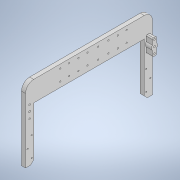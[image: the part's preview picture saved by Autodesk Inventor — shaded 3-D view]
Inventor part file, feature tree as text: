
AUTODESK INVENTOR PART (.ipt)
format: ipt  version: 2020.1 (Build 241239000, 239)  size: 278,528 bytes
history: native  units: in
note: dims shown in document units (in); Inventor stores cm internally (conversion verified against a paired STEP export)
features: sketch x11, extrude x8, mirror x2, chamfer x1, fillet x1, hole x1, projected_geometry x1
ambient origin geometry x8: Origin, YZ Plane, XZ Plane, XY Plane, X Axis, Y Axis, Z Axis, Center Point
bodies: Solid1 (feature_tree)
feature tree (25):
  extrude  "Extrusion1"  Depth=6.44in
  extrude  "Extrusion3"  Depth=0.5in TaperAngle=0.0deg
  chamfer  "Chamfer1"  Distance=1.0in
  extrude  "Extrusion4"  Depth=0.75in
  mirror  "Mirror2"
  extrude  "Extrusion5"  Depth=2.5in
  fillet  "Fillet2"  Radius=1.0in
  extrude  "Extrusion6"  Depth=0.5in
  sketch  "Sketch9"  dims[d19=0.75in d20=0.0in d21=2.5in d22=1.0in d23=0.0in]
  extrude  "Extrusion8"  Depth=0.125in
  mirror  "Mirror3"
  extrude  "Extrusion9"  Depth=0.25in
  extrude  "Extrusion10"  Depth=0.25in
  hole  "Hole1"  [1 undecoded]
  sketch  "Sketch14"  dims[d32=0.75in d33=0.0in d47=0.25in d48=10.0in d49=0.25in d50=0.375in d51=1.0in d52=3.0in d53=3.5in d54=0.5in d55=0.1875in d56=0.25in d57=0.75in d58=1.5938in d59=0.164in d60=0.75in d61=0.0in d62=5.75in d63=1.0in d64=0.0in d65=1.5in d66=0.205in d67=0.205in d68=1.0in d69=0.0in d71=3.17in d72=1.375in d74=0.041in d75=1.083in d76=2.241in d77=0.453in d78=3.51in d79=2.573in d80=2.42in d81=2.268in d82=2.225in d83=0.175in d84=0.75in d85=0.25in d86=0.25in d87=0.5635in d88=0.375in d89=0.8108in d90=5.75in]
  sketch  "Sketch1"  dims[d0=13.6in d1=6.44in]
  sketch  "Sketch3"  dims[d2=1.0in d3=0.5in d4=0.0in]
  sketch  "Sketch4"  dims[d10=0.25in]
  sketch  "Sketch5"  dims[d11=0.5in d13=1.0in d14=0.0in]
  sketch  "Sketch6"  dims[d15=0.375in d16=0.125in d17=45.0deg d18=0.75in]
  sketch  "Sketch10"  dims[d24=1.0in d25=0.5in]
  sketch  "Sketch11"  dims[d26=2.0in d27=0.125in]
  projected_geometry  "Projected Loop1"
  sketch  "Sketch12"  dims[d28=0.207in d29=0.25in]
  sketch  "Sketch13"  dims[d30=0.207in d31=0.25in]
note: 1 required parameter value undecoded (feature->parameter linkage not recoverable at this tier; creation-order binding heuristic only, values carry confidence <= 0.55)
